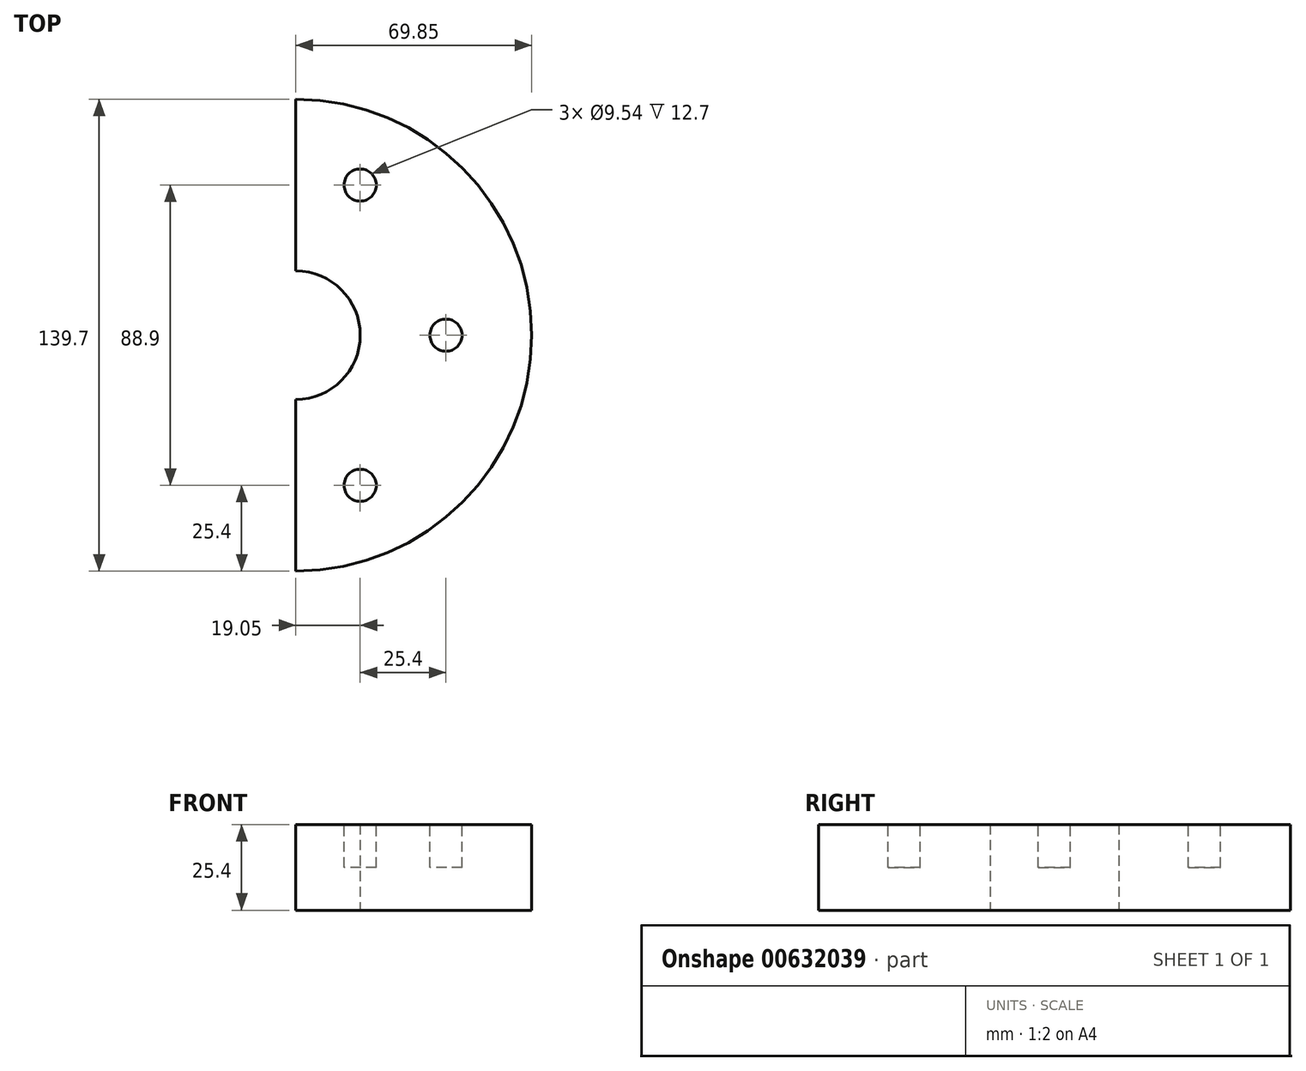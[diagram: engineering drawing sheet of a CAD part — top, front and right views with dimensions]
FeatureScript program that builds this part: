
annotation { "Feature Type Name" : "Feature", "Feature Type Description" : "" }
export const myFeature = defineFeature(function(context is Context, id is Id, definition is map)
    precondition{}
    {
        {
            var Q0;
            Q0=qCreatedBy(makeId("Top.planeOp"),FACE);
            var sketch = newSketch(context, id + "F0", { "sketchPlane" : qUnion([Q0])});
            skArc(sketch, "E0", {"start": v(0, -69.85) * mm, "mid": v(69.85, 0) * mm, "end": v(0, 69.85) * mm});
            skArc(sketch, "E1", {"start": v(0, -19.05) * mm, "mid": v(19.05, 0) * mm, "end": v(0, 19.05) * mm});
            skLineSegment(sketch, "E2", {"start": v(0, 19.05) * mm, "end": v(0, 69.85) * mm});
            skLineSegment(sketch, "E3", {"start": v(0, -19.05) * mm, "end": v(0, -69.85) * mm});
            skSolve(sketch);
        }
        {
            var Q0;
            Q0 = qSketchRegion(id + "F0", true);
            extrude(context, id + "F1", {"entities" : qUnion([Q0]), "depth" : 25.4 * mm, "offsetDistance" : 25.4 * mm});
        }
        {
            var Q0;
            Q0=makeQuery(id+"F1.opExtrude","CAP_FACE",FACE,{"disambiguationData":[OSD([sQuery(id+"F0.wireOp",EDGE,"E0"),sQuery(id+"F0.wireOp",EDGE,"E1"),sQuery(id+"F0.wireOp",EDGE,"E2"),sQuery(id+"F0.wireOp",EDGE,"E3")])],"isStart":false});
            var sketch = newSketch(context, id + "F2", { "sketchPlane" : qUnion([Q0])});
            skCircle(sketch, "E4", {"center": v(19.05, 44.45) * mm, "radius": 4.77 * mm});
            skPoint(sketch, "E4.centerSnap0", {"position": v(0, 44.45) * mm});
            skCircle(sketch, "E5", {"center": v(19.05, -44.45) * mm, "radius": 4.77 * mm});
            skPoint(sketch, "E5.centerSnap0", {"position": v(0, -44.45) * mm});
            skCircle(sketch, "E6", {"center": v(44.45, 0) * mm, "radius": 4.77 * mm});
            skPoint(sketch, "E6.centerSnap0", {"position": v(19.05, 0) * mm});
            skSolve(sketch);
        }
        {
            var Q0;
            Q0 = qSketchRegion(id + "F2", true);
            extrude(context, id + "F3", {"entities" : qUnion([Q0]), "operationType" : NewBodyOperationType.REMOVE, "oppositeDirection" : true, "depth" : 12.7 * mm, "offsetDistance" : 25.4 * mm});
        }
    });
